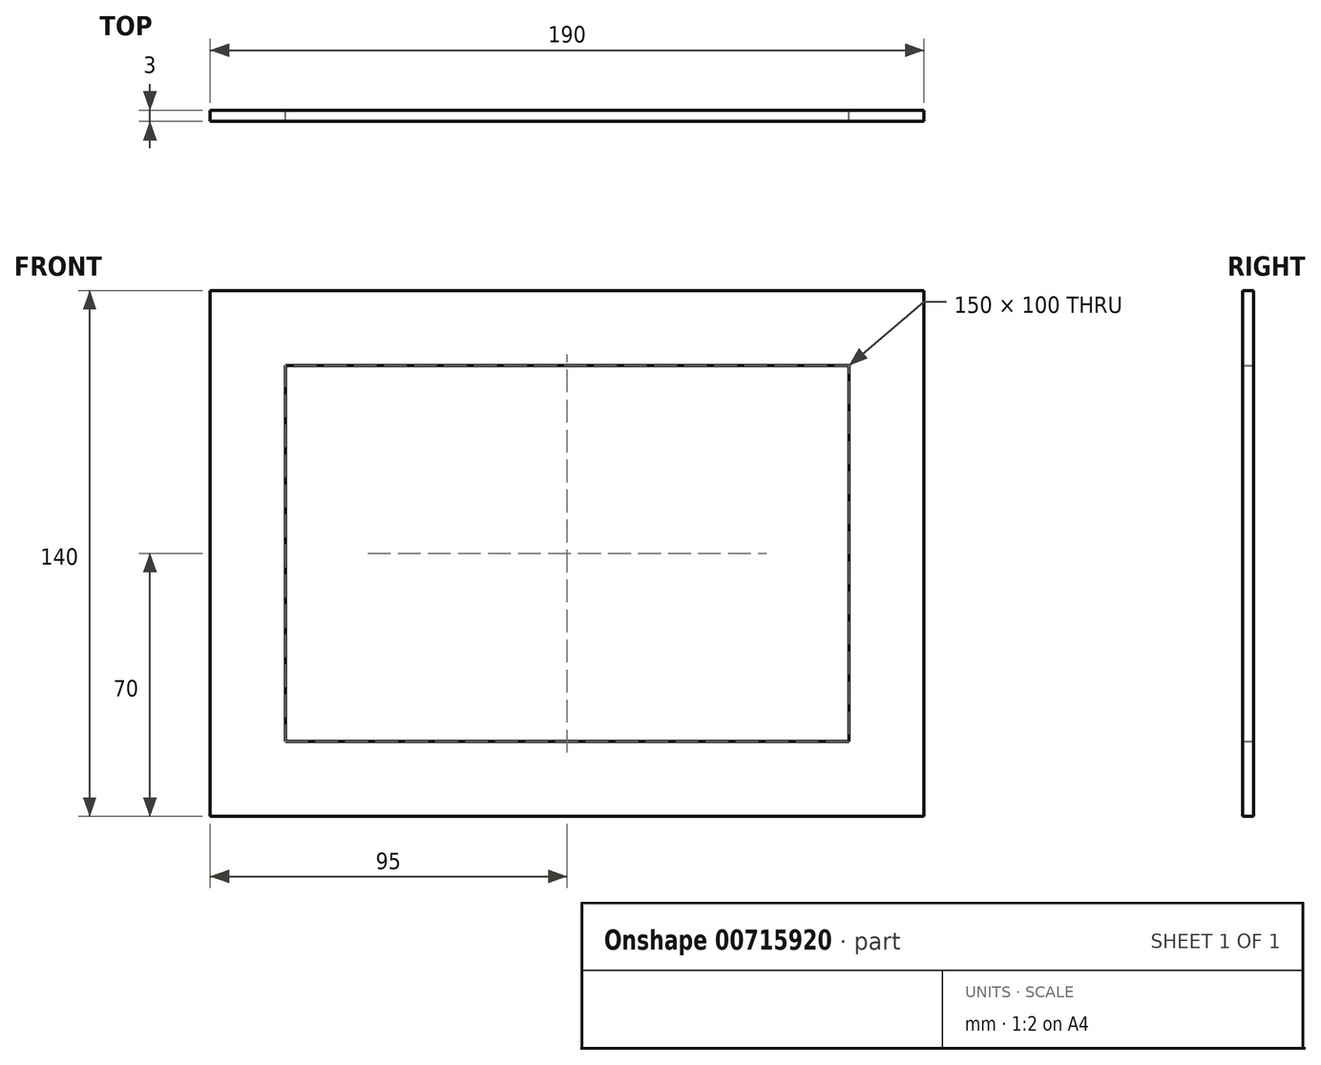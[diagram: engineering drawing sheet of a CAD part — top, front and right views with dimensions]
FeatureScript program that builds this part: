
annotation { "Feature Type Name" : "Feature", "Feature Type Description" : "" }
export const myFeature = defineFeature(function(context is Context, id is Id, definition is map)
    precondition{}
    {
        {
            var Q0;
            Q0=qCreatedBy(makeId("Front.planeOp"),FACE);
            var sketch = newSketch(context, id + "F0", { "sketchPlane" : qUnion([Q0])});
            skLineSegment(sketch, "E0.bottom", {"start": v(-95, 70) * mm, "end": v(95, 70) * mm});
            skLineSegment(sketch, "E0.top", {"start": v(-95, -70) * mm, "end": v(95, -70) * mm});
            skLineSegment(sketch, "E0.left", {"start": v(-95, 70) * mm, "end": v(-95, -70) * mm});
            skLineSegment(sketch, "E0.right", {"start": v(95, 70) * mm, "end": v(95, -70) * mm});
            skPoint(sketch, "E0.middle", {"position": v(0, 0) * mm});
            skLineSegment(sketch, "E1.bottom", {"start": v(-75, 50) * mm, "end": v(75, 50) * mm});
            skLineSegment(sketch, "E1.top", {"start": v(-75, -50) * mm, "end": v(75, -50) * mm});
            skLineSegment(sketch, "E1.left", {"start": v(-75, 50) * mm, "end": v(-75, -50) * mm});
            skLineSegment(sketch, "E1.right", {"start": v(75, 50) * mm, "end": v(75, -50) * mm});
            skLineSegment(sketch, "E2", {"start": v(-95, 70) * mm, "end": v(-75, 50) * mm});
            skLineSegment(sketch, "E3", {"start": v(-75, -50) * mm, "end": v(-95, -70) * mm});
            skLineSegment(sketch, "E4", {"start": v(75, -50) * mm, "end": v(95, -70) * mm});
            skLineSegment(sketch, "E5", {"start": v(75, 50) * mm, "end": v(95, 70) * mm});
            skSolve(sketch);
        }
        {
            var Q0;
            Q0=makeQuery(id+"F0.imprint","IMPRINT",FACE,{"disambiguationData":[TD([[makeQuery(id+"F0.imprint","IMPRINT",EDGE,{"derivedFrom":sQuery(id+"F0.wireOp",EDGE,"E0.left")}),1.0]])]});
            var Q1;
            Q1=makeQuery(id+"F0.imprint","IMPRINT",FACE,{"disambiguationData":[TD([[makeQuery(id+"F0.imprint","IMPRINT",EDGE,{"derivedFrom":sQuery(id+"F0.wireOp",EDGE,"E0.bottom")}),-1.0]])]});
            var Q2;
            Q2=makeQuery(id+"F0.imprint","IMPRINT",FACE,{"disambiguationData":[TD([[makeQuery(id+"F0.imprint","IMPRINT",EDGE,{"derivedFrom":sQuery(id+"F0.wireOp",EDGE,"E0.right")}),-1.0]])]});
            var Q3;
            Q3=makeQuery(id+"F0.imprint","IMPRINT",FACE,{"disambiguationData":[TD([[makeQuery(id+"F0.imprint","IMPRINT",EDGE,{"derivedFrom":sQuery(id+"F0.wireOp",EDGE,"E0.top")}),1.0]])]});
            extrude(context, id + "F1", {"entities" : qUnion([Q0, Q1, Q2, Q3]), "depth" : 3 * mm, "offsetDistance" : 25 * mm});
        }
    });
